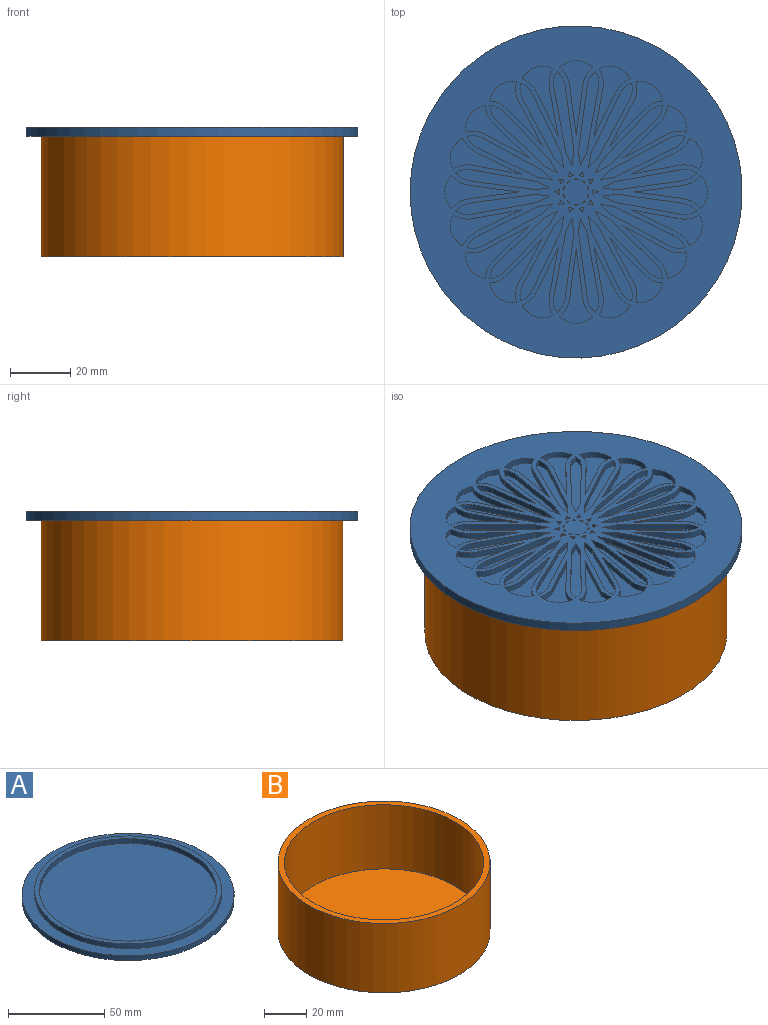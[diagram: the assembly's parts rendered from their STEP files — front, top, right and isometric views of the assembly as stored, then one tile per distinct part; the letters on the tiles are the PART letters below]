
ASSEMBLY  parts=2 mates=1
PART A: 367 faces, bbox 110x110x6 mm
  f0: plane 110x110mm, normal (0,0,-1), area 5849.7mm2, adj f1,f7,f8,f9,f10,f11,f13,f14
  f1: cylinder r=55mm len=110mm, axis (0,0,-1), area 1036.7mm2, adj f0,f2
  f2: plane 110x110mm, normal (0,0,1), area 2113.5mm2, adj f1,f4
  f3: cylinder r=46mm len=92mm, axis (0,0,-1), area 867.1mm2, adj f5,f6
  f4: cylinder r=48.5mm len=97mm, axis (0,0,-1), area 914.2mm2, adj f2,f5
  f5: plane 97x97mm, normal (0,0,1), area 742.2mm2, adj f3,f4
  f6: plane 92x92mm, normal (0,0,1), area 6647.6mm2, adj f3
  f7: cylinder r=9mm len=5.75mm, axis (0,0,-1), area 13.5mm2, adj f0,f8,f11,f12
  f8: cylinder r=7.5mm len=10.82mm, axis (0,0,-1), area 24.2mm2, adj f0,f7,f9,f12
  f9: cylinder r=9mm len=5.75mm, axis (0,0,-1), area 13.5mm2, adj f0,f8,f10,f12
  f10: plane 16.29x2.21mm, normal (-0.13,0.99,0), area 32.9mm2, adj f0,f9,f11,f12
  f11: plane 16.29x2.21mm, normal (-0.13,-0.99,0), area 32.9mm2, adj f0,f7,f10,f12
  f12: plane 24.34x10.82mm, normal (0,0,-1), area 91.4mm2, adj f7,f8,f9,f10,f11
  f13: cylinder r=4mm len=2mm, axis (0,0,-1), area 0.3mm2, adj f0,f14,f17,f18
  f14: cylinder r=2.5mm len=2mm, axis (0,0,-1), area 3.2mm2, adj f0,f13,f15,f18
  f15: cylinder r=4mm len=2mm, axis (0,0,-1), area 0.3mm2, adj f0,f14,f16,f18
  f16: cylinder r=2.5mm len=2mm, axis (0,0,-1), area 3.3mm2, adj f0,f15,f17,f18
  f17: cylinder r=2.5mm len=2mm, axis (0,0,-1), area 3.3mm2, adj f0,f13,f16,f18
  f18: plane 1.77x1.59mm, normal (0,0,-1), area 1.2mm2, adj f13,f14,f15,f16,f17
  f19: cylinder r=2.5mm len=2mm, axis (0,0,-1), area 3.3mm2, adj f0,f20,f23,f24
  f20: cylinder r=4mm len=2mm, axis (0,0,-1), area 0.3mm2, adj f0,f19,f21,f24
  f21: cylinder r=2.5mm len=2mm, axis (0,0,-1), area 3.2mm2, adj f0,f20,f22,f24
  f22: cylinder r=4mm len=2mm, axis (0,0,-1), area 0.3mm2, adj f0,f21,f23,f24
  f23: cylinder r=2.5mm len=2mm, axis (0,0,-1), area 3.3mm2, adj f0,f19,f22,f24
  f24: plane 1.77x1.53mm, normal (0,0,-1), area 1.2mm2, adj f19,f20,f21,f22,f23
  f25: cylinder r=4mm len=2mm, axis (0,0,-1), area 0.3mm2, adj f0,f26,f29,f30
  f26: cylinder r=2.5mm len=2mm, axis (0,0,-1), area 3.2mm2, adj f0,f25,f27,f30
  f27: cylinder r=4mm len=2mm, axis (0,0,-1), area 0.3mm2, adj f0,f26,f28,f30
  f28: cylinder r=2.5mm len=2mm, axis (0,0,-1), area 3.3mm2, adj f0,f27,f29,f30
  f29: cylinder r=2.5mm len=2mm, axis (0,0,-1), area 3.3mm2, adj f0,f25,f28,f30
  f30: plane 1.77x1.53mm, normal (0,0,-1), area 1.2mm2, adj f25,f26,f27,f28,f29
  f31: cylinder r=2.5mm len=2mm, axis (0,0,-1), area 3.3mm2, adj f0,f32,f35,f36
  f32: cylinder r=2.5mm len=2mm, axis (0,0,-1), area 3.3mm2, adj f0,f31,f33,f36
  f33: cylinder r=4mm len=2mm, axis (0,0,-1), area 0.3mm2, adj f0,f32,f34,f36
  f34: cylinder r=2.5mm len=2mm, axis (0,0,-1), area 3.2mm2, adj f0,f33,f35,f36
  f35: cylinder r=4mm len=2mm, axis (0,0,-1), area 0.3mm2, adj f0,f31,f34,f36
  f36: plane 1.77x1.59mm, normal (0,0,-1), area 1.2mm2, adj f31,f32,f33,f34,f35
  f37: cylinder r=2.5mm len=2mm, axis (0,0,-1), area 3.3mm2, adj f0,f38,f41,f42
  f38: cylinder r=4mm len=2mm, axis (0,0,-1), area 0.3mm2, adj f0,f37,f39,f42
  f39: cylinder r=2.5mm len=2mm, axis (0,0,-1), area 3.2mm2, adj f0,f38,f40,f42
  f40: cylinder r=4mm len=2mm, axis (0,0,-1), area 0.3mm2, adj f0,f39,f41,f42
  f41: cylinder r=2.5mm len=2mm, axis (0,0,-1), area 3.3mm2, adj f0,f37,f40,f42
  f42: plane 1.74x1.58mm, normal (0,0,-1), area 1.2mm2, adj f37,f38,f39,f40,f41
  f43: cylinder r=4mm len=2mm, axis (0,0,-1), area 0.3mm2, adj f0,f44,f47,f48
  f44: cylinder r=2.5mm len=2mm, axis (0,0,-1), area 3.3mm2, adj f0,f43,f45,f48
  f45: cylinder r=2.5mm len=2mm, axis (0,0,-1), area 3.3mm2, adj f0,f44,f46,f48
  f46: cylinder r=4mm len=2mm, axis (0,0,-1), area 0.3mm2, adj f0,f45,f47,f48
  f47: cylinder r=2.5mm len=2mm, axis (0,0,-1), area 3.2mm2, adj f0,f43,f46,f48
  f48: plane 1.77x1.59mm, normal (0,0,-1), area 1.2mm2, adj f43,f44,f45,f46,f47
  f49: cylinder r=4mm len=2mm, axis (0,0,-1), area 0.3mm2, adj f0,f50,f53,f54
  f50: cylinder r=2.5mm len=2mm, axis (0,0,-1), area 3.2mm2, adj f0,f49,f51,f54
  f51: cylinder r=4mm len=2mm, axis (0,0,-1), area 0.3mm2, adj f0,f50,f52,f54
  f52: cylinder r=2.5mm len=2mm, axis (0,0,-1), area 3.3mm2, adj f0,f51,f53,f54
  f53: cylinder r=2.5mm len=2mm, axis (0,0,-1), area 3.3mm2, adj f0,f49,f52,f54
  f54: plane 1.77x1.53mm, normal (0,0,-1), area 1.2mm2, adj f49,f50,f51,f52,f53
  f55: cylinder r=4mm len=2mm, axis (0,0,-1), area 0.3mm2, adj f0,f56,f59,f60
  f56: cylinder r=2.5mm len=2mm, axis (0,0,-1), area 3.2mm2, adj f0,f55,f57,f60
  f57: cylinder r=4mm len=2mm, axis (0,0,-1), area 0.3mm2, adj f0,f56,f58,f60
  f58: cylinder r=2.5mm len=2mm, axis (0,0,-1), area 3.3mm2, adj f0,f57,f59,f60
  f59: cylinder r=2.5mm len=2mm, axis (0,0,-1), area 3.3mm2, adj f0,f55,f58,f60
  f60: plane 1.77x1.53mm, normal (0,0,-1), area 1.2mm2, adj f55,f56,f57,f58,f59
  f61: plane 4.21x2.27mm, normal (0.47,0.88,0), area 9.6mm2, adj f0,f62,f66,f67
  f62: plane 4.21x2.27mm, normal (-0.88,-0.47,0), area 9.6mm2, adj f0,f61,f63,f67
  f63: plane 15.81x15.11mm, normal (-0.72,-0.69,0), area 43.7mm2, adj f0,f62,f64,f67
  f64: cylinder r=7.5mm len=4.94mm, axis (0,0,-1), area 11.2mm2, adj f0,f63,f65,f67
  f65: cylinder r=7.5mm len=4.94mm, axis (0,0,-1), area 11.2mm2, adj f0,f64,f66,f67
  f66: plane 15.81x15.11mm, normal (0.69,0.72,0), area 43.7mm2, adj f0,f61,f65,f67
  f67: plane 22.32x22.32mm, normal (0,0,-1), area 90.5mm2, adj f61,f62,f63,f64,f65,f66
  f68: cylinder r=9mm len=6.53mm, axis (0,0,-1), area 13.5mm2, adj f0,f69,f72,f73
  f69: cylinder r=7.5mm len=8.76mm, axis (0,0,-1), area 24.2mm2, adj f0,f68,f70,f73
  f70: cylinder r=9mm len=5.97mm, axis (0,0,-1), area 13.5mm2, adj f0,f69,f71,f73
  f71: plane 11.88x11.36mm, normal (0.72,0.69,0), area 32.9mm2, adj f0,f70,f72,f73
  f72: plane 14.47x7.79mm, normal (-0.88,-0.47,0), area 32.9mm2, adj f0,f68,f71,f73
  f73: plane 21.13x17.33mm, normal (0,0,-1), area 91.4mm2, adj f68,f69,f70,f71,f72
  f74: plane 4.71x2mm, normal (0.18,0.98,0), area 9.6mm2, adj f0,f75,f79,f80
  f75: plane 3.46x3.31mm, normal (-0.69,-0.72,0), area 9.6mm2, adj f0,f74,f76,f80
  f76: plane 19.26x10.36mm, normal (-0.47,-0.88,0), area 43.7mm2, adj f0,f75,f77,f80
  f77: cylinder r=7.5mm len=5.41mm, axis (0,0,-1), area 11.2mm2, adj f0,f76,f78,f80
  f78: cylinder r=7.5mm len=3.99mm, axis (0,0,-1), area 11.2mm2, adj f0,f77,f79,f80
  f79: plane 19.71x9.49mm, normal (0.43,0.9,0), area 43.7mm2, adj f0,f74,f78,f80
  f80: plane 28.13x14.57mm, normal (0,0,-1), area 90.5mm2, adj f74,f75,f76,f77,f78,f79
  f81: cylinder r=9mm len=5.97mm, axis (0,0,-1), area 13.5mm2, adj f0,f82,f85,f86
  f82: cylinder r=7.5mm len=8.76mm, axis (0,0,-1), area 24.2mm2, adj f0,f81,f83,f86
  f83: cylinder r=9mm len=6.53mm, axis (0,0,-1), area 13.5mm2, adj f0,f82,f84,f86
  f84: plane 14.47x7.79mm, normal (0.47,0.88,0), area 32.9mm2, adj f0,f83,f85,f86
  f85: plane 11.88x11.36mm, normal (-0.69,-0.72,0), area 32.9mm2, adj f0,f81,f84,f86
  f86: plane 21.13x17.33mm, normal (0,0,-1), area 91.4mm2, adj f81,f82,f83,f84,f85
  f87: cylinder r=4mm len=2mm, axis (0,0,-1), area 0.3mm2, adj f0,f88,f91,f92
  f88: cylinder r=2.5mm len=2mm, axis (0,0,-1), area 3.2mm2, adj f0,f87,f89,f92
  f89: cylinder r=4mm len=2mm, axis (0,0,-1), area 0.3mm2, adj f0,f88,f90,f92
  f90: cylinder r=2.5mm len=2mm, axis (0,0,-1), area 3.3mm2, adj f0,f89,f91,f92
  f91: cylinder r=2.5mm len=2mm, axis (0,0,-1), area 3.3mm2, adj f0,f87,f90,f92
  f92: plane 1.77x1.59mm, normal (0,0,-1), area 1.2mm2, adj f87,f88,f89,f90,f91
  f93: plane 3.46x3.31mm, normal (0.72,0.69,0), area 9.6mm2, adj f0,f94,f98,f99
  f94: plane 4.71x2mm, normal (-0.98,-0.18,0), area 9.6mm2, adj f0,f93,f95,f99
  f95: plane 19.71x9.49mm, normal (-0.9,-0.43,0), area 43.7mm2, adj f0,f94,f96,f99
  f96: cylinder r=7.5mm len=3.99mm, axis (0,0,-1), area 11.2mm2, adj f0,f95,f97,f99
  f97: cylinder r=7.5mm len=5.41mm, axis (0,0,-1), area 11.2mm2, adj f0,f96,f98,f99
  f98: plane 19.26x10.36mm, normal (0.88,0.47,0), area 43.7mm2, adj f0,f93,f97,f99
  f99: plane 28.13x14.57mm, normal (0,0,-1), area 90.5mm2, adj f93,f94,f95,f96,f97,f98
  f100: cylinder r=9mm len=6.46mm, axis (0,0,-1), area 13.5mm2, adj f0,f101,f104,f105
  f101: cylinder r=7.5mm len=10.29mm, axis (0,0,-1), area 24.2mm2, adj f0,f100,f102,f105
  f102: cylinder r=9mm len=4.82mm, axis (0,0,-1), area 13.5mm2, adj f0,f101,f103,f105
  f103: plane 14.81x7.13mm, normal (0.9,0.43,0), area 32.9mm2, adj f0,f102,f104,f105
  f104: plane 16.17x2.94mm, normal (-0.98,-0.18,0), area 32.9mm2, adj f0,f100,f103,f105
  f105: plane 23.52x11.96mm, normal (0,0,-1), area 91.4mm2, adj f100,f101,f102,f103,f104
  f106: plane 4.74x2mm, normal (-0.99,0.13,0), area 9.6mm2, adj f0,f107,f111,f112
  f107: plane 21.67x2.94mm, normal (-0.99,-0.13,0), area 43.7mm2, adj f0,f106,f108,f112
  f108: cylinder r=7.5mm len=4.77mm, axis (0,0,-1), area 11.2mm2, adj f0,f107,f109,f112
  f109: cylinder r=7.5mm len=5.35mm, axis (0,0,-1), area 11.2mm2, adj f0,f108,f110,f112
  f110: plane 21.52x3.91mm, normal (0.98,0.18,0), area 43.7mm2, adj f0,f109,f111,f112
  f111: plane 4.31x2.08mm, normal (0.9,0.43,0), area 9.6mm2, adj f0,f106,f110,f112
  f112: plane 31.18x6.74mm, normal (0,0,-1), area 90.5mm2, adj f106,f107,f108,f109,f110,f111
  f113: cylinder r=4mm len=2mm, axis (0,0,-1), area 1.5mm2, adj f0,f114,f115,f116
  f114: cylinder r=4mm len=2mm, axis (0,0,-1), area 1.5mm2, adj f0,f113,f115,f116
  f115: cylinder r=4mm len=2mm, axis (0,0,-1), area 2.6mm2, adj f0,f113,f114,f116
  f116: plane 1.28x0.46mm, normal (0,0,-1), area 0.3mm2, adj f113,f114,f115
  f117: cylinder r=4mm len=2mm, axis (0,0,-1), area 1.5mm2, adj f0,f118,f119,f120
  f118: cylinder r=4mm len=2mm, axis (0,0,-1), area 2.6mm2, adj f0,f117,f119,f120
  f119: cylinder r=4mm len=2mm, axis (0,0,-1), area 1.5mm2, adj f0,f117,f118,f120
  f120: plane 1.04x0.75mm, normal (0,0,-1), area 0.3mm2, adj f117,f118,f119
  f121: cylinder r=4mm len=2mm, axis (0,0,-1), area 1.5mm2, adj f0,f122,f123,f124
  f122: cylinder r=4mm len=2mm, axis (0,0,-1), area 2.6mm2, adj f0,f121,f123,f124
  f123: cylinder r=4mm len=2mm, axis (0,0,-1), area 1.5mm2, adj f0,f121,f122,f124
  f124: plane 1.22x0.59mm, normal (0,0,-1), area 0.3mm2, adj f121,f122,f123
  f125: cylinder r=4mm len=2mm, axis (0,0,-1), area 1.5mm2, adj f0,f126,f127,f128
  f126: cylinder r=4mm len=2mm, axis (0,0,-1), area 2.6mm2, adj f0,f125,f127,f128
  f127: cylinder r=4mm len=2mm, axis (0,0,-1), area 1.5mm2, adj f0,f125,f126,f128
  f128: plane 1.22x0.59mm, normal (0,0,-1), area 0.3mm2, adj f125,f126,f127
  f129: cylinder r=4mm len=2mm, axis (0,0,-1), area 1.5mm2, adj f0,f130,f131,f132
  f130: cylinder r=4mm len=2mm, axis (0,0,-1), area 2.6mm2, adj f0,f129,f131,f132
  f131: cylinder r=4mm len=2mm, axis (0,0,-1), area 1.5mm2, adj f0,f129,f130,f132
  f132: plane 1.22x0.59mm, normal (0,0,-1), area 0.3mm2, adj f129,f130,f131
  f133: cylinder r=4mm len=2mm, axis (0,0,-1), area 1.5mm2, adj f0,f134,f135,f136
  f134: cylinder r=4mm len=2mm, axis (0,0,-1), area 2.6mm2, adj f0,f133,f135,f136
  f135: cylinder r=4mm len=2mm, axis (0,0,-1), area 1.5mm2, adj f0,f133,f134,f136
  f136: plane 1.04x0.75mm, normal (0,0,-1), area 0.3mm2, adj f133,f134,f135
  f137: cylinder r=4mm len=2mm, axis (0,0,-1), area 0.3mm2, adj f0,f138,f141,f142
  f138: cylinder r=2.5mm len=2mm, axis (0,0,-1), area 3.2mm2, adj f0,f137,f139,f142
  f139: cylinder r=4mm len=2mm, axis (0,0,-1), area 0.3mm2, adj f0,f138,f140,f142
  f140: cylinder r=2.5mm len=2mm, axis (0,0,-1), area 3.3mm2, adj f0,f139,f141,f142
  f141: cylinder r=2.5mm len=2mm, axis (0,0,-1), area 3.3mm2, adj f0,f137,f140,f142
  f142: plane 1.74x1.58mm, normal (0,0,-1), area 1.2mm2, adj f137,f138,f139,f140,f141
  f143: cylinder r=4mm len=2mm, axis (0,0,-1), area 1.5mm2, adj f0,f144,f145,f146
  f144: cylinder r=4mm len=2mm, axis (0,0,-1), area 2.6mm2, adj f0,f143,f145,f146
  f145: cylinder r=4mm len=2mm, axis (0,0,-1), area 1.5mm2, adj f0,f143,f144,f146
  f146: plane 1.04x0.75mm, normal (0,0,-1), area 0.3mm2, adj f143,f144,f145
  f147: cylinder r=4mm len=2mm, axis (0,0,-1), area 1.5mm2, adj f0,f148,f149,f150
  f148: cylinder r=4mm len=2mm, axis (0,0,-1), area 2.6mm2, adj f0,f147,f149,f150
  f149: cylinder r=4mm len=2mm, axis (0,0,-1), area 1.5mm2, adj f0,f147,f148,f150
  f150: plane 1.28x0.46mm, normal (0,0,-1), area 0.3mm2, adj f147,f148,f149
  f151: cylinder r=4mm len=2mm, axis (0,0,-1), area 1.5mm2, adj f0,f152,f153,f154
  f152: cylinder r=4mm len=2mm, axis (0,0,-1), area 2.6mm2, adj f0,f151,f153,f154
  f153: cylinder r=4mm len=2mm, axis (0,0,-1), area 1.5mm2, adj f0,f151,f152,f154
  f154: plane 1.04x0.75mm, normal (0,0,-1), area 0.3mm2, adj f151,f152,f153
  f155: cylinder r=4mm len=2mm, axis (0,0,-1), area 1.5mm2, adj f0,f156,f157,f158
  f156: cylinder r=4mm len=2mm, axis (0,0,-1), area 2.6mm2, adj f0,f155,f157,f158
  f157: cylinder r=4mm len=2mm, axis (0,0,-1), area 1.5mm2, adj f0,f155,f156,f158
  f158: plane 1.22x0.59mm, normal (0,0,-1), area 0.3mm2, adj f155,f156,f157
  f159: plane 4.31x2.08mm, normal (-0.9,-0.43,0), area 9.6mm2, adj f0,f160,f164,f165
  f160: plane 4.74x2mm, normal (0.99,-0.13,0), area 9.6mm2, adj f0,f159,f161,f165
  f161: plane 21.67x2.94mm, normal (0.99,0.13,0), area 43.7mm2, adj f0,f160,f162,f165
  f162: cylinder r=7.5mm len=4.77mm, axis (0,0,-1), area 11.2mm2, adj f0,f161,f163,f165
  f163: cylinder r=7.5mm len=5.35mm, axis (0,0,-1), area 11.2mm2, adj f0,f162,f164,f165
  f164: plane 21.52x3.91mm, normal (-0.98,-0.18,0), area 43.7mm2, adj f0,f159,f163,f165
  f165: plane 31.18x6.74mm, normal (0,0,-1), area 90.5mm2, adj f159,f160,f161,f162,f163,f164
  f166: cylinder r=9mm len=6.46mm, axis (0,0,-1), area 13.5mm2, adj f0,f167,f170,f171
  f167: cylinder r=7.5mm len=10.29mm, axis (0,0,-1), area 24.2mm2, adj f0,f166,f168,f171
  f168: cylinder r=9mm len=4.82mm, axis (0,0,-1), area 13.5mm2, adj f0,f167,f169,f171
  f169: plane 14.81x7.13mm, normal (-0.9,-0.43,0), area 32.9mm2, adj f0,f168,f170,f171
  f170: plane 16.17x2.94mm, normal (0.98,0.18,0), area 32.9mm2, adj f0,f166,f169,f171
  f171: plane 23.52x11.96mm, normal (0,0,-1), area 91.4mm2, adj f166,f167,f168,f169,f170
  f172: cylinder r=9mm len=5.75mm, axis (0,0,-1), area 13.5mm2, adj f0,f173,f176,f177
  f173: cylinder r=7.5mm len=10.82mm, axis (0,0,-1), area 24.2mm2, adj f0,f172,f174,f177
  f174: cylinder r=9mm len=5.75mm, axis (0,0,-1), area 13.5mm2, adj f0,f173,f175,f177
  f175: plane 16.29x2.21mm, normal (-0.99,-0.13,0), area 32.9mm2, adj f0,f174,f176,f177
  f176: plane 16.29x2.21mm, normal (0.99,-0.13,0), area 32.9mm2, adj f0,f172,f175,f177
  f177: plane 24.34x10.82mm, normal (0,0,-1), area 91.4mm2, adj f172,f173,f174,f175,f176
  f178: cylinder r=9mm len=6.46mm, axis (0,0,-1), area 13.5mm2, adj f0,f179,f182,f183
  f179: plane 16.17x2.94mm, normal (-0.98,0.18,0), area 32.9mm2, adj f0,f178,f180,f183
  f180: plane 14.81x7.13mm, normal (0.9,-0.43,0), area 32.9mm2, adj f0,f179,f181,f183
  f181: cylinder r=9mm len=4.82mm, axis (0,0,-1), area 13.5mm2, adj f0,f180,f182,f183
  f182: cylinder r=7.5mm len=10.29mm, axis (0,0,-1), area 24.2mm2, adj f0,f178,f181,f183
  f183: plane 23.52x11.96mm, normal (0,0,-1), area 91.4mm2, adj f178,f179,f180,f181,f182
  f184: cylinder r=7.5mm len=4.94mm, axis (0,0,-1), area 11.2mm2, adj f0,f185,f189,f190
  f185: cylinder r=7.5mm len=4.94mm, axis (0,0,-1), area 11.2mm2, adj f0,f184,f186,f190
  f186: plane 15.81x15.11mm, normal (-0.69,-0.72,0), area 43.7mm2, adj f0,f185,f187,f190
  f187: plane 4.21x2.27mm, normal (-0.47,-0.88,0), area 9.6mm2, adj f0,f186,f188,f190
  f188: plane 4.21x2.27mm, normal (0.88,0.47,0), area 9.6mm2, adj f0,f187,f189,f190
  f189: plane 15.81x15.11mm, normal (0.72,0.69,0), area 43.7mm2, adj f0,f184,f188,f190
  f190: plane 22.32x22.32mm, normal (0,0,-1), area 90.5mm2, adj f184,f185,f186,f187,f188,f189
  f191: plane 14.47x7.79mm, normal (-0.47,-0.88,0), area 32.9mm2, adj f0,f192,f195,f196
  f192: plane 11.88x11.36mm, normal (0.69,0.72,0), area 32.9mm2, adj f0,f191,f193,f196
  f193: cylinder r=9mm len=5.97mm, axis (0,0,-1), area 13.5mm2, adj f0,f192,f194,f196
  f194: cylinder r=7.5mm len=8.76mm, axis (0,0,-1), area 24.2mm2, adj f0,f193,f195,f196
  f195: cylinder r=9mm len=6.53mm, axis (0,0,-1), area 13.5mm2, adj f0,f191,f194,f196
  f196: plane 21.13x17.33mm, normal (0,0,-1), area 91.4mm2, adj f191,f192,f193,f194,f195
  f197: plane 4.71x2mm, normal (0.98,0.18,0), area 9.6mm2, adj f0,f198,f202,f203
  f198: plane 19.71x9.49mm, normal (0.9,0.43,0), area 43.7mm2, adj f0,f197,f199,f203
  f199: cylinder r=7.5mm len=3.99mm, axis (0,0,-1), area 11.2mm2, adj f0,f198,f200,f203
  f200: cylinder r=7.5mm len=5.41mm, axis (0,0,-1), area 11.2mm2, adj f0,f199,f201,f203
  f201: plane 19.26x10.36mm, normal (-0.88,-0.47,0), area 43.7mm2, adj f0,f200,f202,f203
  f202: plane 3.46x3.31mm, normal (-0.72,-0.69,0), area 9.6mm2, adj f0,f197,f201,f203
  f203: plane 28.13x14.57mm, normal (0,0,-1), area 90.5mm2, adj f197,f198,f199,f200,f201,f202
  f204: cylinder r=9mm len=6.53mm, axis (0,0,-1), area 13.5mm2, adj f0,f205,f208,f209
  f205: cylinder r=7.5mm len=8.76mm, axis (0,0,-1), area 24.2mm2, adj f0,f204,f206,f209
  f206: cylinder r=9mm len=5.97mm, axis (0,0,-1), area 13.5mm2, adj f0,f205,f207,f209
  f207: plane 11.88x11.36mm, normal (-0.72,-0.69,0), area 32.9mm2, adj f0,f206,f208,f209
  f208: plane 14.47x7.79mm, normal (0.88,0.47,0), area 32.9mm2, adj f0,f204,f207,f209
  f209: plane 21.13x17.33mm, normal (0,0,-1), area 91.4mm2, adj f204,f205,f206,f207,f208
  f210: plane 4.71x2mm, normal (0.18,-0.98,0), area 9.6mm2, adj f0,f211,f215,f216
  f211: plane 19.71x9.49mm, normal (0.43,-0.9,0), area 43.7mm2, adj f0,f210,f212,f216
  f212: cylinder r=7.5mm len=3.99mm, axis (0,0,-1), area 11.2mm2, adj f0,f211,f213,f216
  f213: cylinder r=7.5mm len=5.41mm, axis (0,0,-1), area 11.2mm2, adj f0,f212,f214,f216
  f214: plane 19.26x10.36mm, normal (-0.47,0.88,0), area 43.7mm2, adj f0,f213,f215,f216
  f215: plane 3.46x3.31mm, normal (-0.69,0.72,0), area 9.6mm2, adj f0,f210,f214,f216
  f216: plane 28.13x14.57mm, normal (0,0,-1), area 90.5mm2, adj f210,f211,f212,f213,f214,f215
  f217: cylinder r=9mm len=6.53mm, axis (0,0,-1), area 13.5mm2, adj f0,f218,f221,f222
  f218: cylinder r=7.5mm len=8.76mm, axis (0,0,-1), area 24.2mm2, adj f0,f217,f219,f222
  f219: cylinder r=9mm len=5.97mm, axis (0,0,-1), area 13.5mm2, adj f0,f218,f220,f222
  f220: plane 11.88x11.36mm, normal (-0.69,0.72,0), area 32.9mm2, adj f0,f219,f221,f222
  f221: plane 14.47x7.79mm, normal (0.47,-0.88,0), area 32.9mm2, adj f0,f217,f220,f222
  f222: plane 21.13x17.33mm, normal (0,0,-1), area 91.4mm2, adj f217,f218,f219,f220,f221
  f223: plane 14.81x7.13mm, normal (-0.43,0.9,0), area 32.9mm2, adj f0,f224,f227,f228
  f224: plane 16.17x2.94mm, normal (0.18,-0.98,0), area 32.9mm2, adj f0,f223,f225,f228
  f225: cylinder r=9mm len=6.46mm, axis (0,0,-1), area 13.5mm2, adj f0,f224,f226,f228
  f226: cylinder r=7.5mm len=10.29mm, axis (0,0,-1), area 24.2mm2, adj f0,f225,f227,f228
  f227: cylinder r=9mm len=4.82mm, axis (0,0,-1), area 13.5mm2, adj f0,f223,f226,f228
  f228: plane 23.52x11.96mm, normal (0,0,-1), area 91.4mm2, adj f223,f224,f225,f226,f227
  f229: plane 4.31x2.08mm, normal (-0.43,0.9,0), area 9.6mm2, adj f0,f230,f234,f235
  f230: plane 4.74x2mm, normal (-0.13,-0.99,0), area 9.6mm2, adj f0,f229,f231,f235
  f231: plane 21.67x2.94mm, normal (0.13,-0.99,0), area 43.7mm2, adj f0,f230,f232,f235
  f232: cylinder r=7.5mm len=4.77mm, axis (0,0,-1), area 11.2mm2, adj f0,f231,f233,f235
  f233: cylinder r=7.5mm len=5.35mm, axis (0,0,-1), area 11.2mm2, adj f0,f232,f234,f235
  f234: plane 21.52x3.91mm, normal (-0.18,0.98,0), area 43.7mm2, adj f0,f229,f233,f235
  f235: plane 31.18x6.74mm, normal (0,0,-1), area 90.5mm2, adj f229,f230,f231,f232,f233,f234
  f236: plane 4.71x2mm, normal (-0.98,0.18,0), area 9.6mm2, adj f0,f237,f241,f242
  f237: plane 3.46x3.31mm, normal (0.72,-0.69,0), area 9.6mm2, adj f0,f236,f238,f242
  f238: plane 19.26x10.36mm, normal (0.88,-0.47,0), area 43.7mm2, adj f0,f237,f239,f242
  f239: cylinder r=7.5mm len=5.41mm, axis (0,0,-1), area 11.2mm2, adj f0,f238,f240,f242
  f240: cylinder r=7.5mm len=3.99mm, axis (0,0,-1), area 11.2mm2, adj f0,f239,f241,f242
  f241: plane 19.71x9.49mm, normal (-0.9,0.43,0), area 43.7mm2, adj f0,f236,f240,f242
  f242: plane 28.13x14.57mm, normal (0,0,-1), area 90.5mm2, adj f236,f237,f238,f239,f240,f241
  f243: plane 4.74x2mm, normal (-0.99,-0.13,0), area 9.6mm2, adj f0,f244,f248,f249
  f244: plane 4.31x2.08mm, normal (0.9,-0.43,0), area 9.6mm2, adj f0,f243,f245,f249
  f245: plane 21.52x3.91mm, normal (0.98,-0.18,0), area 43.7mm2, adj f0,f244,f246,f249
  f246: cylinder r=7.5mm len=5.35mm, axis (0,0,-1), area 11.2mm2, adj f0,f245,f247,f249
  f247: cylinder r=7.5mm len=4.77mm, axis (0,0,-1), area 11.2mm2, adj f0,f246,f248,f249
  f248: plane 21.67x2.94mm, normal (-0.99,0.13,0), area 43.7mm2, adj f0,f243,f247,f249
  f249: plane 31.18x6.74mm, normal (0,0,-1), area 90.5mm2, adj f243,f244,f245,f246,f247,f248
  f250: plane 4.21x2.27mm, normal (-0.88,0.47,0), area 9.6mm2, adj f0,f251,f255,f256
  f251: plane 4.21x2.27mm, normal (0.47,-0.88,0), area 9.6mm2, adj f0,f250,f252,f256
  f252: plane 15.81x15.11mm, normal (0.69,-0.72,0), area 43.7mm2, adj f0,f251,f253,f256
  f253: cylinder r=7.5mm len=4.94mm, axis (0,0,-1), area 11.2mm2, adj f0,f252,f254,f256
  f254: cylinder r=7.5mm len=4.94mm, axis (0,0,-1), area 11.2mm2, adj f0,f253,f255,f256
  f255: plane 15.81x15.11mm, normal (-0.72,0.69,0), area 43.7mm2, adj f0,f250,f254,f256
  f256: plane 22.32x22.32mm, normal (0,0,-1), area 90.5mm2, adj f250,f251,f252,f253,f254,f255
  f257: cylinder r=9mm len=5.97mm, axis (0,0,-1), area 13.5mm2, adj f0,f258,f261,f262
  f258: cylinder r=7.5mm len=8.76mm, axis (0,0,-1), area 24.2mm2, adj f0,f257,f259,f262
  f259: cylinder r=9mm len=6.53mm, axis (0,0,-1), area 13.5mm2, adj f0,f258,f260,f262
  f260: plane 14.47x7.79mm, normal (-0.88,0.47,0), area 32.9mm2, adj f0,f259,f261,f262
  f261: plane 11.88x11.36mm, normal (0.72,-0.69,0), area 32.9mm2, adj f0,f257,f260,f262
  f262: plane 21.13x17.33mm, normal (0,0,-1), area 91.4mm2, adj f257,f258,f259,f260,f261
  f263: plane 4.71x2mm, normal (0.98,-0.18,0), area 9.6mm2, adj f0,f264,f268,f269
  f264: plane 3.46x3.31mm, normal (-0.72,0.69,0), area 9.6mm2, adj f0,f263,f265,f269
  f265: plane 19.26x10.36mm, normal (-0.88,0.47,0), area 43.7mm2, adj f0,f264,f266,f269
  f266: cylinder r=7.5mm len=5.41mm, axis (0,0,-1), area 11.2mm2, adj f0,f265,f267,f269
  f267: cylinder r=7.5mm len=3.99mm, axis (0,0,-1), area 11.2mm2, adj f0,f266,f268,f269
  f268: plane 19.71x9.49mm, normal (0.9,-0.43,0), area 43.7mm2, adj f0,f263,f267,f269
  f269: plane 28.13x14.57mm, normal (0,0,-1), area 90.5mm2, adj f263,f264,f265,f266,f267,f268
  f270: plane 16.17x2.94mm, normal (0.98,-0.18,0), area 32.9mm2, adj f0,f271,f274,f275
  f271: plane 14.81x7.13mm, normal (-0.9,0.43,0), area 32.9mm2, adj f0,f270,f272,f275
  f272: cylinder r=9mm len=4.82mm, axis (0,0,-1), area 13.5mm2, adj f0,f271,f273,f275
  f273: cylinder r=7.5mm len=10.29mm, axis (0,0,-1), area 24.2mm2, adj f0,f272,f274,f275
  f274: cylinder r=9mm len=6.46mm, axis (0,0,-1), area 13.5mm2, adj f0,f270,f273,f275
  f275: plane 23.52x11.96mm, normal (0,0,-1), area 91.4mm2, adj f270,f271,f272,f273,f274
  f276: plane 4.21x2.27mm, normal (0.88,-0.47,0), area 9.6mm2, adj f0,f277,f281,f282
  f277: plane 4.21x2.27mm, normal (-0.47,0.88,0), area 9.6mm2, adj f0,f276,f278,f282
  f278: plane 15.81x15.11mm, normal (-0.69,0.72,0), area 43.7mm2, adj f0,f277,f279,f282
  f279: cylinder r=7.5mm len=4.94mm, axis (0,0,-1), area 11.2mm2, adj f0,f278,f280,f282
  f280: cylinder r=7.5mm len=4.94mm, axis (0,0,-1), area 11.2mm2, adj f0,f279,f281,f282
  f281: plane 15.81x15.11mm, normal (0.72,-0.69,0), area 43.7mm2, adj f0,f276,f280,f282
  f282: plane 22.32x22.32mm, normal (0,0,-1), area 90.5mm2, adj f276,f277,f278,f279,f280,f281
  f283: plane 14.47x7.79mm, normal (0.88,-0.47,0), area 32.9mm2, adj f0,f284,f287,f288
  f284: plane 11.88x11.36mm, normal (-0.72,0.69,0), area 32.9mm2, adj f0,f283,f285,f288
  f285: cylinder r=9mm len=5.97mm, axis (0,0,-1), area 13.5mm2, adj f0,f284,f286,f288
  f286: cylinder r=7.5mm len=8.76mm, axis (0,0,-1), area 24.2mm2, adj f0,f285,f287,f288
  f287: cylinder r=9mm len=6.53mm, axis (0,0,-1), area 13.5mm2, adj f0,f283,f286,f288
  f288: plane 21.13x17.33mm, normal (0,0,-1), area 91.4mm2, adj f283,f284,f285,f286,f287
  f289: cylinder r=9mm len=5.75mm, axis (0,0,-1), area 13.5mm2, adj f0,f290,f293,f294
  f290: plane 16.29x2.21mm, normal (0.99,0.13,0), area 32.9mm2, adj f0,f289,f291,f294
  f291: plane 16.29x2.21mm, normal (-0.99,0.13,0), area 32.9mm2, adj f0,f290,f292,f294
  f292: cylinder r=9mm len=5.75mm, axis (0,0,-1), area 13.5mm2, adj f0,f291,f293,f294
  f293: cylinder r=7.5mm len=10.82mm, axis (0,0,-1), area 24.2mm2, adj f0,f289,f292,f294
  f294: plane 24.34x10.82mm, normal (0,0,-1), area 91.4mm2, adj f289,f290,f291,f292,f293
  f295: plane 4.74x2mm, normal (0.99,0.13,0), area 9.6mm2, adj f0,f296,f300,f301
  f296: plane 4.31x2.08mm, normal (-0.9,0.43,0), area 9.6mm2, adj f0,f295,f297,f301
  f297: plane 21.52x3.91mm, normal (-0.98,0.18,0), area 43.7mm2, adj f0,f296,f298,f301
  f298: cylinder r=7.5mm len=5.35mm, axis (0,0,-1), area 11.2mm2, adj f0,f297,f299,f301
  f299: cylinder r=7.5mm len=4.77mm, axis (0,0,-1), area 11.2mm2, adj f0,f298,f300,f301
  f300: plane 21.67x2.94mm, normal (0.99,-0.13,0), area 43.7mm2, adj f0,f295,f299,f301
  f301: plane 31.18x6.74mm, normal (0,0,-1), area 90.5mm2, adj f295,f296,f297,f298,f299,f300
  f302: cylinder r=9mm len=4.82mm, axis (0,0,-1), area 13.5mm2, adj f0,f303,f306,f307
  f303: cylinder r=7.5mm len=10.29mm, axis (0,0,-1), area 24.2mm2, adj f0,f302,f304,f307
  f304: cylinder r=9mm len=6.46mm, axis (0,0,-1), area 13.5mm2, adj f0,f303,f305,f307
  f305: plane 16.17x2.94mm, normal (0.18,0.98,0), area 32.9mm2, adj f0,f304,f306,f307
  f306: plane 14.81x7.13mm, normal (-0.43,-0.9,0), area 32.9mm2, adj f0,f302,f305,f307
  f307: plane 23.52x11.96mm, normal (0,0,-1), area 91.4mm2, adj f302,f303,f304,f305,f306
  f308: plane 4.74x2mm, normal (-0.13,0.99,0), area 9.6mm2, adj f0,f309,f313,f314
  f309: plane 4.31x2.08mm, normal (-0.43,-0.9,0), area 9.6mm2, adj f0,f308,f310,f314
  f310: plane 21.52x3.91mm, normal (-0.18,-0.98,0), area 43.7mm2, adj f0,f309,f311,f314
  f311: cylinder r=7.5mm len=5.35mm, axis (0,0,-1), area 11.2mm2, adj f0,f310,f312,f314
  f312: cylinder r=7.5mm len=4.77mm, axis (0,0,-1), area 11.2mm2, adj f0,f311,f313,f314
  f313: plane 21.67x2.94mm, normal (0.13,0.99,0), area 43.7mm2, adj f0,f308,f312,f314
  f314: plane 31.18x6.74mm, normal (0,0,-1), area 90.5mm2, adj f308,f309,f310,f311,f312,f313
  f315: plane 4.74x2mm, normal (0.13,-0.99,0), area 9.6mm2, adj f0,f316,f320,f321
  f316: plane 4.31x2.08mm, normal (0.43,0.9,0), area 9.6mm2, adj f0,f315,f317,f321
  f317: plane 21.52x3.91mm, normal (0.18,0.98,0), area 43.7mm2, adj f0,f316,f318,f321
  f318: cylinder r=7.5mm len=5.35mm, axis (0,0,-1), area 11.2mm2, adj f0,f317,f319,f321
  f319: cylinder r=7.5mm len=4.77mm, axis (0,0,-1), area 11.2mm2, adj f0,f318,f320,f321
  f320: plane 21.67x2.94mm, normal (-0.13,-0.99,0), area 43.7mm2, adj f0,f315,f319,f321
  f321: plane 31.18x6.74mm, normal (0,0,-1), area 90.5mm2, adj f315,f316,f317,f318,f319,f320
  f322: cylinder r=9mm len=5.75mm, axis (0,0,-1), area 13.5mm2, adj f0,f323,f326,f327
  f323: plane 16.29x2.21mm, normal (0.13,-0.99,0), area 32.9mm2, adj f0,f322,f324,f327
  f324: plane 16.29x2.21mm, normal (0.13,0.99,0), area 32.9mm2, adj f0,f323,f325,f327
  f325: cylinder r=9mm len=5.75mm, axis (0,0,-1), area 13.5mm2, adj f0,f324,f326,f327
  f326: cylinder r=7.5mm len=10.82mm, axis (0,0,-1), area 24.2mm2, adj f0,f322,f325,f327
  f327: plane 24.34x10.82mm, normal (0,0,-1), area 91.4mm2, adj f322,f323,f324,f325,f326
  f328: plane 4.71x2mm, normal (-0.18,-0.98,0), area 9.6mm2, adj f0,f329,f333,f334
  f329: plane 3.46x3.31mm, normal (0.69,0.72,0), area 9.6mm2, adj f0,f328,f330,f334
  f330: plane 19.26x10.36mm, normal (0.47,0.88,0), area 43.7mm2, adj f0,f329,f331,f334
  f331: cylinder r=7.5mm len=5.41mm, axis (0,0,-1), area 11.2mm2, adj f0,f330,f332,f334
  f332: cylinder r=7.5mm len=3.99mm, axis (0,0,-1), area 11.2mm2, adj f0,f331,f333,f334
  f333: plane 19.71x9.49mm, normal (-0.43,-0.9,0), area 43.7mm2, adj f0,f328,f332,f334
  f334: plane 28.13x14.57mm, normal (0,0,-1), area 90.5mm2, adj f328,f329,f330,f331,f332,f333
  f335: cylinder r=9mm len=6.46mm, axis (0,0,-1), area 13.5mm2, adj f0,f336,f339,f340
  f336: plane 16.17x2.94mm, normal (-0.18,-0.98,0), area 32.9mm2, adj f0,f335,f337,f340
  f337: plane 14.81x7.13mm, normal (0.43,0.9,0), area 32.9mm2, adj f0,f336,f338,f340
  f338: cylinder r=9mm len=4.82mm, axis (0,0,-1), area 13.5mm2, adj f0,f337,f339,f340
  f339: cylinder r=7.5mm len=10.29mm, axis (0,0,-1), area 24.2mm2, adj f0,f335,f338,f340
  f340: plane 23.52x11.96mm, normal (0,0,-1), area 91.4mm2, adj f335,f336,f337,f338,f339
  f341: plane 3.46x3.31mm, normal (0.69,-0.72,0), area 9.6mm2, adj f0,f342,f346,f347
  f342: plane 4.71x2mm, normal (-0.18,0.98,0), area 9.6mm2, adj f0,f341,f343,f347
  f343: plane 19.71x9.49mm, normal (-0.43,0.9,0), area 43.7mm2, adj f0,f342,f344,f347
  f344: cylinder r=7.5mm len=3.99mm, axis (0,0,-1), area 11.2mm2, adj f0,f343,f345,f347
  f345: cylinder r=7.5mm len=5.41mm, axis (0,0,-1), area 11.2mm2, adj f0,f344,f346,f347
  f346: plane 19.26x10.36mm, normal (0.47,-0.88,0), area 43.7mm2, adj f0,f341,f345,f347
  f347: plane 28.13x14.57mm, normal (0,0,-1), area 90.5mm2, adj f341,f342,f343,f344,f345,f346
  f348: cylinder r=9mm len=5.97mm, axis (0,0,-1), area 13.5mm2, adj f0,f349,f352,f353
  f349: plane 11.88x11.36mm, normal (0.69,-0.72,0), area 32.9mm2, adj f0,f348,f350,f353
  f350: plane 14.47x7.79mm, normal (-0.47,0.88,0), area 32.9mm2, adj f0,f349,f351,f353
  f351: cylinder r=9mm len=6.53mm, axis (0,0,-1), area 13.5mm2, adj f0,f350,f352,f353
  f352: cylinder r=7.5mm len=8.76mm, axis (0,0,-1), area 24.2mm2, adj f0,f348,f351,f353
  f353: plane 21.13x17.33mm, normal (0,0,-1), area 91.4mm2, adj f348,f349,f350,f351,f352
  f354: plane 21.67x2.94mm, normal (-0.13,0.99,0), area 43.7mm2, adj f0,f355,f359,f360
  f355: cylinder r=7.5mm len=4.77mm, axis (0,0,-1), area 11.2mm2, adj f0,f354,f356,f360
  f356: cylinder r=7.5mm len=5.35mm, axis (0,0,-1), area 11.2mm2, adj f0,f355,f357,f360
  f357: plane 21.52x3.91mm, normal (0.18,-0.98,0), area 43.7mm2, adj f0,f356,f358,f360
  f358: plane 4.31x2.08mm, normal (0.43,-0.9,0), area 9.6mm2, adj f0,f357,f359,f360
  f359: plane 4.74x2mm, normal (0.13,0.99,0), area 9.6mm2, adj f0,f354,f358,f360
  f360: plane 31.18x6.74mm, normal (0,0,-1), area 90.5mm2, adj f354,f355,f356,f357,f358,f359
  f361: cylinder r=9mm len=6.46mm, axis (0,0,-1), area 13.5mm2, adj f0,f362,f365,f366
  f362: cylinder r=7.5mm len=10.29mm, axis (0,0,-1), area 24.2mm2, adj f0,f361,f363,f366
  f363: cylinder r=9mm len=4.82mm, axis (0,0,-1), area 13.5mm2, adj f0,f362,f364,f366
  f364: plane 14.81x7.13mm, normal (0.43,-0.9,0), area 32.9mm2, adj f0,f363,f365,f366
  f365: plane 16.17x2.94mm, normal (-0.18,0.98,0), area 32.9mm2, adj f0,f361,f364,f366
  f366: plane 23.52x11.96mm, normal (0,0,-1), area 91.4mm2, adj f361,f362,f363,f364,f365
PART B: 5 faces, bbox 100x100x40 mm
  f0: cylinder r=50mm len=100mm, axis (0,0,-1), area 12566.4mm2, adj f1,f2
  f1: plane 100x100mm, normal (0,0,1), area 914.2mm2, adj f0,f3
  f2: plane 100x100mm, normal (0,0,-1), area 7854mm2, adj f0
  f3: cylinder r=47mm len=94mm, axis (0,0,-1), area 10926.5mm2, adj f1,f4
  f4: plane 94x94mm, normal (0,0,1), area 6939.8mm2, adj f3
PLACE A rot(axis=(0,1,0),180deg) t=(0,0,61.8)mm
PLACE B rot(axis=(0,-1,0),0deg) t=(0,0,18.8)mm
MATE fastened B.f0 <-> A.f1  axis (0,0,1) through (0,0,58.8)mm
